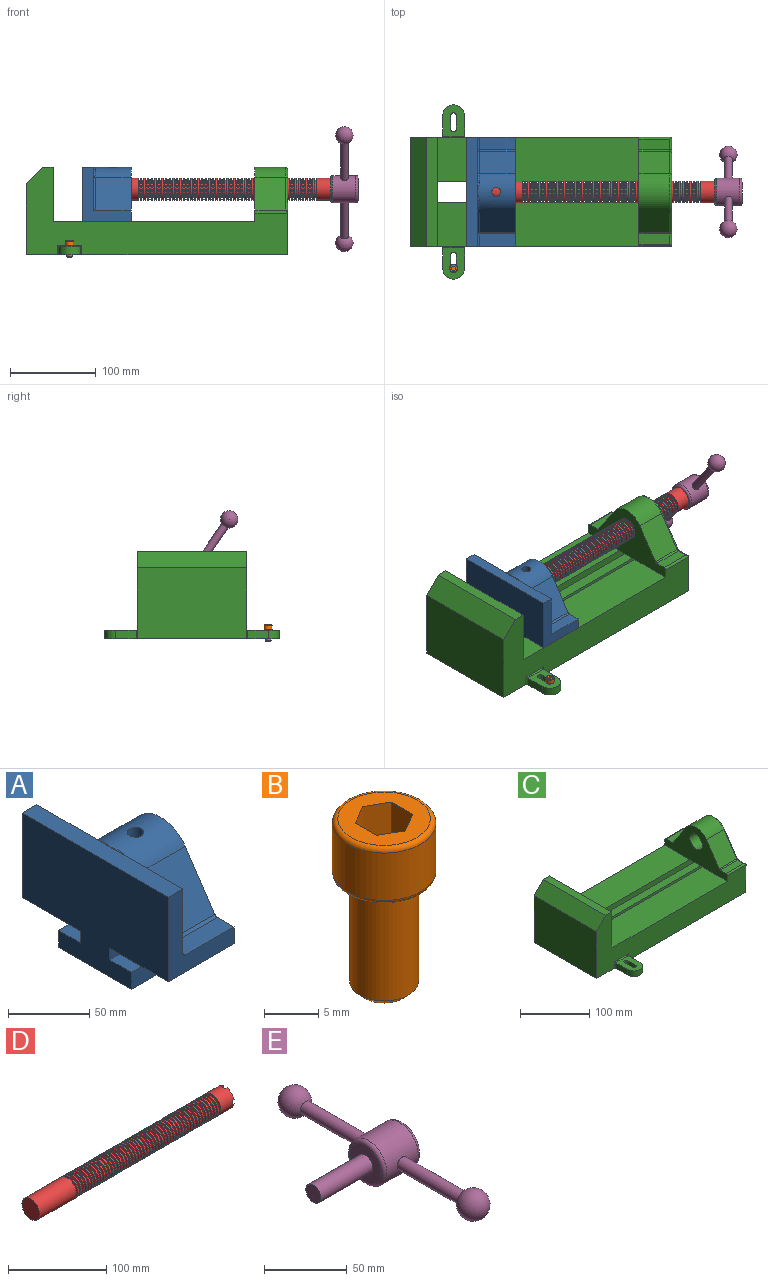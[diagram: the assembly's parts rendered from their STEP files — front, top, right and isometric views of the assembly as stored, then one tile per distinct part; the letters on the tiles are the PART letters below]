
ASSEMBLY  parts=5 mates=5
PART A: 36 faces, bbox 57.2x127x89 mm
  f0: plane 57.15x50.8mm, normal (0,0,-1), area 2903.2mm2, adj f6,f9,f10,f23
  f1: cylinder r=12.7mm len=44.45mm, axis (1,0,0), area 3464.3mm2, adj f6,f15,f16
  f2: plane 41.91x14.52mm, normal (0,0,1), area 608.5mm2, adj f6,f11,f24,f25
  f3: plane 51.86x48.26mm, normal (1,0,0), area 1495.7mm2, adj f8,f10,f31,f33,f35
  f4: plane 51.86x48.26mm, normal (1,0,0), area 1495.7mm2, adj f8,f11,f24,f28,f29
  f5: plane 57.15x50.8mm, normal (0,0,-1), area 2903.2mm2, adj f6,f9,f11,f22
  f6: plane 127x85.09mm, normal (1,0,0), area 5190.6mm2, adj f0,f1,f2,f5,f7,f10,f11,f12
  f7: plane 41.91x14.52mm, normal (0,0,1), area 608.5mm2, adj f6,f10,f30,f31
  f8: plane 127x12.7mm, normal (0,0,1), area 1612.9mm2, adj f3,f4,f9,f10,f11,f26,f34
  f9: plane 127x85.09mm, normal (-1,0,0), area 9096.8mm2, adj f0,f5,f8,f10,f11,f17,f18,f19
  f10: plane 63.5x57.15mm, normal (0,-1,0), area 1372.3mm2, adj f0,f3,f6,f7,f8,f9,f31
  f11: plane 63.5x57.15mm, normal (0,1,0), area 1372.3mm2, adj f2,f4,f5,f6,f8,f9,f24
  f12: plane 41.91x38.43mm, normal (0,-0.83,0.56), area 1939.2mm2, adj f6,f13,f30,f33
  f13: cylinder r=25.4mm len=44.45mm, axis (1,0,0), area 2026.5mm2, adj f6,f12,f14,f16,f26,f28,f34,f35
  f14: plane 41.91x38.43mm, normal (0,0.83,0.56), area 1939.2mm2, adj f6,f13,f25,f29
  f15: plane 25.4x25.4mm, normal (1,0,0), area 506.7mm2, adj f1
  f16: cylinder r=5.08mm len=13.76mm, axis (0,0,1), area 414mm2, adj f1,f13
  f17: plane 57.15x19.05mm, normal (0,0,1), area 1088.7mm2, adj f6,f9,f18,f23
  f18: plane 57.15x12.7mm, normal (0,-1,0), area 725.8mm2, adj f6,f9,f17,f19
  f19: plane 63.5x57.15mm, normal (0,0,-1), area 3629mm2, adj f6,f9,f18,f20
  f20: plane 57.15x12.7mm, normal (0,1,0), area 725.8mm2, adj f6,f9,f19,f21
  f21: plane 57.15x19.05mm, normal (0,0,1), area 1088.7mm2, adj f6,f9,f20,f22
  f22: plane 57.15x8.89mm, normal (0,1,0), area 508.1mm2, adj f5,f6,f9,f21
  f23: plane 57.15x8.89mm, normal (0,-1,0), area 508.1mm2, adj f0,f6,f9,f17
  f24: cylinder r=2.54mm len=14.52mm, axis (0,-1,0), area 57.9mm2, adj f2,f4,f11,f27
  f25: cylinder r=2.54mm len=41.91mm, axis (1,0,0), area 104.3mm2, adj f2,f6,f14,f27
  f26: bspline ~12.24x2.8mm, area 20.9mm2, adj f8,f13,f28
  f27: sphere r=2.54mm, area 6.3mm2, adj f24,f25,f29
  f28: torus R=27.94mm, axis (1,0,0), area 57.8mm2, adj f4,f13,f26,f29
  f29: cylinder r=2.54mm len=39.84mm, axis (0,-0.56,0.83), area 184.6mm2, adj f4,f14,f27,f28
  f30: cylinder r=2.54mm len=41.91mm, axis (1,0,0), area 104.3mm2, adj f6,f7,f12,f32
  f31: cylinder r=2.54mm len=14.52mm, axis (0,-1,0), area 57.9mm2, adj f3,f7,f10,f32
  f32: sphere r=2.54mm, area 6.3mm2, adj f30,f31,f33
  f33: cylinder r=2.54mm len=39.84mm, axis (0,-0.56,-0.83), area 184.6mm2, adj f3,f12,f32,f35
  f34: bspline ~12.24x2.8mm, area 20.9mm2, adj f8,f13,f35
  f35: torus R=27.94mm, axis (1,0,0), area 57.8mm2, adj f3,f13,f33,f34
PART B: 15 faces, bbox 10.3x10.3x19.1 mm
  f0: plane 8.51x8.51mm, normal (0,0,1), area 37.2mm2, adj f5,f6,f7,f8,f9,f10,f14
  f1: cylinder r=3.17mm len=11.94mm, axis (0,0,1), area 238.2mm2, adj f4,f12
  f2: plane 4.83x4.83mm, normal (0,0,-1), area 18.3mm2, adj f12
  f3: cylinder r=4.76mm len=9.53mm, axis (0,0,-1), area 159.6mm2, adj f13,f14
  f4: plane 8.51x8.51mm, normal (0,0,-1), area 25.2mm2, adj f1,f13
  f5: plane 4.83x2.38mm, normal (-0.5,-0.87,0), area 13.3mm2, adj f0,f6,f10,f11
  f6: plane 4.83x2.38mm, normal (0.5,-0.87,0), area 13.3mm2, adj f0,f5,f7,f11
  f7: plane 4.83x2.75mm, normal (1,0,0), area 13.3mm2, adj f0,f6,f8,f11
  f8: plane 4.83x2.38mm, normal (0.5,0.87,0), area 13.3mm2, adj f0,f7,f9,f11
  f9: plane 4.83x2.38mm, normal (-0.5,0.87,0), area 13.3mm2, adj f0,f8,f10,f11
  f10: plane 4.83x2.75mm, normal (-1,0,0), area 13.3mm2, adj f0,f5,f9,f11
  f11: plane 5.5x4.76mm, normal (0,0,1), area 19.6mm2, adj f5,f6,f7,f8,f9,f10
  f12: cone r=3.17mm half-angle=45deg, axis (0,0,1), area 18.9mm2, adj f1,f2
  f13: torus R=4.25mm, axis (0,0,1), area 23mm2, adj f3,f4
  f14: torus R=4.25mm, axis (0,0,1), area 23mm2, adj f0,f3
PART C: 61 faces, bbox 304.8x203.2x103.7 mm
  f0: plane 304.8x101.6mm, normal (0,1,0), area 13520.3mm2, adj f3,f4,f5,f6,f7,f8,f9,f16
  f1: plane 304.8x101.6mm, normal (0,-1,0), area 13520.3mm2, adj f2,f3,f5,f6,f7,f8,f9,f16
  f2: plane 234.95x50.8mm, normal (0,0,1), area 11935.5mm2, adj f1,f5,f16,f26
  f3: plane 127x99.06mm, normal (1,0,0), area 7097.5mm2, adj f0,f1,f9,f14,f17,f18,f19,f20
  f4: plane 234.95x50.8mm, normal (0,0,1), area 11935.5mm2, adj f0,f5,f16,f27
  f5: plane 127x101.6mm, normal (1,0,0), area 9516.1mm2, adj f0,f1,f2,f4,f6,f9,f18,f19
  f6: plane 127x12.7mm, normal (0,0,1), area 1612.9mm2, adj f0,f1,f5,f7
  f7: plane 127x19.05mm, normal (-0.71,0,0.71), area 3421.5mm2, adj f0,f1,f6,f8
  f8: plane 127x82.55mm, normal (-1,0,0), area 10483.8mm2, adj f0,f1,f7,f9
  f9: plane 304.8x203.2mm, normal (0,0,-1), area 33298.3mm2, adj f0,f1,f3,f5,f8,f21,f22,f39
  f10: plane 35.56x11.98mm, normal (0,0,1), area 426mm2, adj f16,f28,f29,f30
  f11: plane 38.43x35.56mm, normal (0,0.83,0.56), area 1645.4mm2, adj f12,f16,f29,f32
  f12: cylinder r=25.4mm len=42.19mm, axis (1,0,0), area 1770.2mm2, adj f11,f13,f16,f33
  f13: plane 38.43x35.56mm, normal (0,-0.83,0.56), area 1645.4mm2, adj f12,f16,f34,f35
  f14: cylinder r=12.7mm len=38.1mm, axis (1,0,0), area 3040.2mm2, adj f3,f16
  f15: plane 35.56x11.98mm, normal (0,0,1), area 426mm2, adj f16,f34,f36,f38
  f16: plane 127x63.5mm, normal (-1,0,0), area 4155.5mm2, adj f0,f1,f2,f4,f10,f11,f12,f13
  f17: plane 38.1x25.4mm, normal (0,0,-1), area 967.7mm2, adj f3,f16,f26,f27
  f18: plane 273.05x19.05mm, normal (0,0,-1), area 5201.6mm2, adj f3,f5,f19,f26
  f19: plane 273.05x12.7mm, normal (0,1,0), area 3467.7mm2, adj f3,f5,f18,f20
  f20: plane 273.05x19.05mm, normal (0,0,1), area 5201.6mm2, adj f3,f5,f19,f21
  f21: plane 273.05x16.51mm, normal (0,1,0), area 4508.1mm2, adj f3,f5,f9,f20
  f22: plane 273.05x16.51mm, normal (0,-1,0), area 4508.1mm2, adj f3,f5,f9,f23
  f23: plane 273.05x19.05mm, normal (0,0,1), area 5201.6mm2, adj f3,f5,f22,f24
  f24: plane 273.05x12.7mm, normal (0,-1,0), area 3467.7mm2, adj f3,f5,f23,f25
  f25: plane 273.05x19.05mm, normal (0,0,-1), area 5201.6mm2, adj f3,f5,f24,f27
  f26: plane 273.05x8.89mm, normal (0,1,0), area 2427.4mm2, adj f2,f3,f5,f17,f18
  f27: plane 273.05x8.89mm, normal (0,-1,0), area 2427.4mm2, adj f3,f4,f5,f17,f25
  f28: cylinder r=2.54mm len=38.1mm, axis (1,0,0), area 148.3mm2, adj f0,f10,f16,f30
  f29: cylinder r=2.54mm len=35.56mm, axis (-1,0,0), area 88.5mm2, adj f10,f11,f16,f31
  f30: cylinder r=2.54mm len=14.52mm, axis (0,1,0), area 54.3mm2, adj f3,f10,f28,f31
  f31: torus R=5.08mm, axis (-1,0,0), area 13.5mm2, adj f3,f29,f30,f32
  f32: cylinder r=2.54mm len=39.84mm, axis (0,0.56,-0.83), area 184.6mm2, adj f3,f11,f31,f33
  f33: torus R=22.86mm, axis (-1,0,0), area 191.4mm2, adj f3,f12,f32,f35
  f34: cylinder r=2.54mm len=35.56mm, axis (-1,0,0), area 88.5mm2, adj f13,f15,f16,f37
  f35: cylinder r=2.54mm len=39.84mm, axis (0,0.56,0.83), area 184.6mm2, adj f3,f13,f33,f37
  f36: cylinder r=2.54mm len=38.1mm, axis (-1,0,0), area 148.3mm2, adj f1,f15,f16,f38
  f37: torus R=5.08mm, axis (-1,0,0), area 13.5mm2, adj f3,f34,f35,f38
  f38: cylinder r=2.54mm len=14.52mm, axis (0,1,0), area 54.3mm2, adj f3,f15,f36,f37
  f39: plane 23.88x9.53mm, normal (-1,0,0), area 227.4mm2, adj f9,f45,f46,f60
  f40: plane 23.88x9.53mm, normal (1,0,0), area 227.4mm2, adj f9,f45,f46,f58
  f41: cylinder r=3.3mm len=9.53mm, axis (0,0,-1), area 98.8mm2, adj f9,f42,f44,f46
  f42: plane 15.62x9.53mm, normal (-1,0,0), area 148.8mm2, adj f9,f41,f43,f46
  f43: cylinder r=3.3mm len=9.53mm, axis (0,0,-1), area 98.8mm2, adj f9,f42,f44,f46
  f44: plane 15.62x9.53mm, normal (1,0,0), area 148.8mm2, adj f9,f41,f43,f46
  f45: cylinder r=12.7mm len=25.4mm, axis (0,0,-1), area 380mm2, adj f9,f39,f40,f46
  f46: plane 36.58x25.4mm, normal (0,0,1), area 722.4mm2, adj f39,f40,f41,f42,f43,f44,f45,f59
  f47: plane 23.88x9.53mm, normal (-1,0,0), area 227.4mm2, adj f9,f53,f54,f56
  f48: plane 23.88x9.53mm, normal (1,0,0), area 227.4mm2, adj f9,f53,f54,f55
  f49: cylinder r=3.3mm len=9.53mm, axis (0,0,-1), area 98.8mm2, adj f9,f50,f52,f54
  f50: plane 15.62x9.53mm, normal (-1,0,0), area 148.8mm2, adj f9,f49,f51,f54
  f51: cylinder r=3.3mm len=9.53mm, axis (0,0,-1), area 98.8mm2, adj f9,f50,f52,f54
  f52: plane 15.62x9.53mm, normal (1,0,0), area 148.8mm2, adj f9,f49,f51,f54
  f53: cylinder r=12.7mm len=25.4mm, axis (0,0,-1), area 380mm2, adj f9,f47,f48,f54
  f54: plane 36.58x25.4mm, normal (0,0,1), area 722.4mm2, adj f47,f48,f49,f50,f51,f52,f53,f57
  f55: cylinder r=1.52mm len=11.05mm, axis (0,0,-1), area 24.1mm2, adj f0,f9,f48,f57
  f56: cylinder r=1.52mm len=11.05mm, axis (0,0,1), area 24.1mm2, adj f0,f9,f47,f57
  f57: cylinder r=1.52mm len=28.45mm, axis (1,0,0), area 63.5mm2, adj f0,f54,f55,f56
  f58: cylinder r=1.52mm len=11.05mm, axis (0,0,1), area 24.1mm2, adj f1,f9,f40,f59
  f59: cylinder r=1.52mm len=28.45mm, axis (-1,0,0), area 63.5mm2, adj f1,f46,f58,f60
  f60: cylinder r=1.52mm len=11.05mm, axis (0,0,-1), area 24.1mm2, adj f1,f9,f39,f59
PART D: 220 faces, bbox 279.4x25.4x25.4 mm
  f0: cylinder r=12.7mm len=25.4mm, axis (-1,0,0), area 1468.2mm2, adj f1,f2,f3,f5,f7,f208,f209,f210
  f1: plane 9.9x9.9mm, normal (1,0,0), area 62.3mm2, adj f0,f4,f213,f216
  f2: plane 9.9x9.9mm, normal (1,0,0), area 62.3mm2, adj f0,f4,f210,f218
  f3: plane 9.9x9.9mm, normal (1,0,0), area 62.3mm2, adj f0,f4,f209,f212
  f4: cylinder r=6.35mm len=25.4mm, axis (1,0,0), area 960.3mm2, adj f1,f2,f3,f5,f6,f208,f209,f210
  f5: plane 9.9x9.9mm, normal (1,0,0), area 62.3mm2, adj f0,f4,f215,f217
  f6: plane 12.7x12.7mm, normal (1,0,0), area 126.7mm2, adj f4
  f7: cone r=12.7mm half-angle=76deg, axis (1,0,0), area 188mm2, adj f0,f9
  f8: cone r=10.16mm half-angle=76deg, axis (-1,0,0), area 188mm2, adj f9,f10
  f9: cylinder r=10.16mm len=20.32mm, axis (1,0,0), area 81.1mm2, adj f7,f8
  f10: cylinder r=12.7mm len=25.4mm, axis (-1,0,0), area 131.7mm2, adj f8,f11
  f11: cone r=12.7mm half-angle=76deg, axis (1,0,0), area 188mm2, adj f10,f13
  f12: cone r=10.16mm half-angle=76deg, axis (-1,0,0), area 188mm2, adj f13,f14
  f13: cylinder r=10.16mm len=20.32mm, axis (1,0,0), area 81.1mm2, adj f11,f12
  f14: cylinder r=12.7mm len=25.4mm, axis (-1,0,0), area 131.7mm2, adj f12,f15
  f15: cone r=12.7mm half-angle=76deg, axis (1,0,0), area 188mm2, adj f14,f17
  f16: cone r=10.16mm half-angle=76deg, axis (-1,0,0), area 188mm2, adj f17,f18
  f17: cylinder r=10.16mm len=20.32mm, axis (1,0,0), area 81.1mm2, adj f15,f16
  f18: cylinder r=12.7mm len=25.4mm, axis (-1,0,0), area 131.7mm2, adj f16,f19
  f19: cone r=12.7mm half-angle=76deg, axis (1,0,0), area 188mm2, adj f18,f21
  f20: cone r=10.16mm half-angle=76deg, axis (-1,0,0), area 188mm2, adj f21,f22
  f21: cylinder r=10.16mm len=20.32mm, axis (1,0,0), area 81.1mm2, adj f19,f20
  f22: cylinder r=12.7mm len=25.4mm, axis (-1,0,0), area 131.7mm2, adj f20,f23
  f23: cone r=12.7mm half-angle=76deg, axis (1,0,0), area 188mm2, adj f22,f25
  f24: cone r=10.16mm half-angle=76deg, axis (-1,0,0), area 188mm2, adj f25,f26
  f25: cylinder r=10.16mm len=20.32mm, axis (1,0,0), area 81.1mm2, adj f23,f24
  f26: cylinder r=12.7mm len=25.4mm, axis (-1,0,0), area 131.7mm2, adj f24,f27
  f27: cone r=12.7mm half-angle=76deg, axis (1,0,0), area 188mm2, adj f26,f29
  f28: cone r=10.16mm half-angle=76deg, axis (-1,0,0), area 188mm2, adj f29,f30
  f29: cylinder r=10.16mm len=20.32mm, axis (1,0,0), area 81.1mm2, adj f27,f28
  f30: cylinder r=12.7mm len=25.4mm, axis (-1,0,0), area 131.7mm2, adj f28,f31
  f31: cone r=12.7mm half-angle=76deg, axis (1,0,0), area 188mm2, adj f30,f33
  f32: cone r=10.16mm half-angle=76deg, axis (-1,0,0), area 188mm2, adj f33,f34
  f33: cylinder r=10.16mm len=20.32mm, axis (1,0,0), area 81.1mm2, adj f31,f32
  f34: cylinder r=12.7mm len=25.4mm, axis (-1,0,0), area 131.7mm2, adj f32,f35
  f35: cone r=12.7mm half-angle=76deg, axis (1,0,0), area 188mm2, adj f34,f37
  f36: cone r=10.16mm half-angle=76deg, axis (-1,0,0), area 188mm2, adj f37,f38
  f37: cylinder r=10.16mm len=20.32mm, axis (1,0,0), area 81.1mm2, adj f35,f36
  f38: cylinder r=12.7mm len=25.4mm, axis (-1,0,0), area 131.7mm2, adj f36,f39
  f39: cone r=12.7mm half-angle=76deg, axis (1,0,0), area 188mm2, adj f38,f41
  f40: cone r=10.16mm half-angle=76deg, axis (-1,0,0), area 188mm2, adj f41,f42
  f41: cylinder r=10.16mm len=20.32mm, axis (1,0,0), area 81.1mm2, adj f39,f40
  f42: cylinder r=12.7mm len=25.4mm, axis (-1,0,0), area 131.7mm2, adj f40,f43
  f43: cone r=12.7mm half-angle=76deg, axis (1,0,0), area 188mm2, adj f42,f45
  f44: cone r=10.16mm half-angle=76deg, axis (-1,0,0), area 188mm2, adj f45,f46
  f45: cylinder r=10.16mm len=20.32mm, axis (1,0,0), area 81.1mm2, adj f43,f44
  f46: cylinder r=12.7mm len=25.4mm, axis (-1,0,0), area 131.7mm2, adj f44,f47
  f47: cone r=12.7mm half-angle=76deg, axis (1,0,0), area 188mm2, adj f46,f49
  f48: cone r=10.16mm half-angle=76deg, axis (-1,0,0), area 188mm2, adj f49,f50
  f49: cylinder r=10.16mm len=20.32mm, axis (1,0,0), area 81.1mm2, adj f47,f48
  f50: cylinder r=12.7mm len=25.4mm, axis (-1,0,0), area 131.7mm2, adj f48,f51
  f51: cone r=12.7mm half-angle=76deg, axis (1,0,0), area 188mm2, adj f50,f53
  f52: cone r=10.16mm half-angle=76deg, axis (-1,0,0), area 188mm2, adj f53,f54
  f53: cylinder r=10.16mm len=20.32mm, axis (1,0,0), area 81.1mm2, adj f51,f52
  f54: cylinder r=12.7mm len=25.4mm, axis (-1,0,0), area 131.7mm2, adj f52,f55
  f55: cone r=12.7mm half-angle=76deg, axis (1,0,0), area 188mm2, adj f54,f57
  f56: cone r=10.16mm half-angle=76deg, axis (-1,0,0), area 188mm2, adj f57,f58
  f57: cylinder r=10.16mm len=20.32mm, axis (1,0,0), area 81.1mm2, adj f55,f56
  f58: cylinder r=12.7mm len=25.4mm, axis (-1,0,0), area 131.7mm2, adj f56,f59
  f59: cone r=12.7mm half-angle=76deg, axis (1,0,0), area 188mm2, adj f58,f61
  f60: cone r=10.16mm half-angle=76deg, axis (-1,0,0), area 188mm2, adj f61,f62
  f61: cylinder r=10.16mm len=20.32mm, axis (1,0,0), area 81.1mm2, adj f59,f60
  f62: cylinder r=12.7mm len=25.4mm, axis (-1,0,0), area 131.7mm2, adj f60,f63
  f63: cone r=12.7mm half-angle=76deg, axis (1,0,0), area 188mm2, adj f62,f65
  f64: cone r=10.16mm half-angle=76deg, axis (-1,0,0), area 188mm2, adj f65,f66
  f65: cylinder r=10.16mm len=20.32mm, axis (1,0,0), area 81.1mm2, adj f63,f64
  f66: cylinder r=12.7mm len=25.4mm, axis (-1,0,0), area 131.7mm2, adj f64,f67
  f67: cone r=12.7mm half-angle=76deg, axis (1,0,0), area 188mm2, adj f66,f69
  f68: cone r=10.16mm half-angle=76deg, axis (-1,0,0), area 188mm2, adj f69,f70
  f69: cylinder r=10.16mm len=20.32mm, axis (1,0,0), area 81.1mm2, adj f67,f68
  f70: cylinder r=12.7mm len=25.4mm, axis (-1,0,0), area 131.7mm2, adj f68,f71
  f71: cone r=12.7mm half-angle=76deg, axis (1,0,0), area 188mm2, adj f70,f73
  f72: cone r=10.16mm half-angle=76deg, axis (-1,0,0), area 188mm2, adj f73,f74
  f73: cylinder r=10.16mm len=20.32mm, axis (1,0,0), area 81.1mm2, adj f71,f72
  f74: cylinder r=12.7mm len=25.4mm, axis (-1,0,0), area 131.7mm2, adj f72,f75
  f75: cone r=12.7mm half-angle=76deg, axis (1,0,0), area 188mm2, adj f74,f77
  f76: cone r=10.16mm half-angle=76deg, axis (-1,0,0), area 188mm2, adj f77,f78
  f77: cylinder r=10.16mm len=20.32mm, axis (1,0,0), area 81.1mm2, adj f75,f76
  f78: cylinder r=12.7mm len=25.4mm, axis (-1,0,0), area 131.7mm2, adj f76,f79
  f79: cone r=12.7mm half-angle=76deg, axis (1,0,0), area 188mm2, adj f78,f81
  f80: cone r=10.16mm half-angle=76deg, axis (-1,0,0), area 188mm2, adj f81,f82
  f81: cylinder r=10.16mm len=20.32mm, axis (1,0,0), area 81.1mm2, adj f79,f80
  f82: cylinder r=12.7mm len=25.4mm, axis (-1,0,0), area 131.7mm2, adj f80,f83
  f83: cone r=12.7mm half-angle=76deg, axis (1,0,0), area 188mm2, adj f82,f85
  f84: cone r=10.16mm half-angle=76deg, axis (-1,0,0), area 188mm2, adj f85,f86
  f85: cylinder r=10.16mm len=20.32mm, axis (1,0,0), area 81.1mm2, adj f83,f84
  f86: cylinder r=12.7mm len=25.4mm, axis (-1,0,0), area 131.7mm2, adj f84,f87
  f87: cone r=12.7mm half-angle=76deg, axis (1,0,0), area 188mm2, adj f86,f89
  f88: cone r=10.16mm half-angle=76deg, axis (-1,0,0), area 188mm2, adj f89,f90
  f89: cylinder r=10.16mm len=20.32mm, axis (1,0,0), area 81.1mm2, adj f87,f88
  f90: cylinder r=12.7mm len=25.4mm, axis (-1,0,0), area 131.7mm2, adj f88,f91
  f91: cone r=12.7mm half-angle=76deg, axis (1,0,0), area 188mm2, adj f90,f93
  f92: cone r=10.16mm half-angle=76deg, axis (-1,0,0), area 188mm2, adj f93,f94
  f93: cylinder r=10.16mm len=20.32mm, axis (1,0,0), area 81.1mm2, adj f91,f92
  f94: cylinder r=12.7mm len=25.4mm, axis (-1,0,0), area 131.7mm2, adj f92,f95
  f95: cone r=12.7mm half-angle=76deg, axis (1,0,0), area 188mm2, adj f94,f97
  f96: cone r=10.16mm half-angle=76deg, axis (-1,0,0), area 188mm2, adj f97,f98
  f97: cylinder r=10.16mm len=20.32mm, axis (1,0,0), area 81.1mm2, adj f95,f96
  f98: cylinder r=12.7mm len=25.4mm, axis (-1,0,0), area 131.7mm2, adj f96,f99
  f99: cone r=12.7mm half-angle=76deg, axis (1,0,0), area 188mm2, adj f98,f101
  f100: cone r=10.16mm half-angle=76deg, axis (-1,0,0), area 188mm2, adj f101,f102
  f101: cylinder r=10.16mm len=20.32mm, axis (1,0,0), area 81.1mm2, adj f99,f100
  f102: cylinder r=12.7mm len=25.4mm, axis (-1,0,0), area 131.7mm2, adj f100,f103
  f103: cone r=12.7mm half-angle=76deg, axis (1,0,0), area 188mm2, adj f102,f105
  f104: cone r=10.16mm half-angle=76deg, axis (-1,0,0), area 188mm2, adj f105,f106
  f105: cylinder r=10.16mm len=20.32mm, axis (1,0,0), area 81.1mm2, adj f103,f104
  f106: cylinder r=12.7mm len=25.4mm, axis (-1,0,0), area 131.7mm2, adj f104,f107
  f107: cone r=12.7mm half-angle=76deg, axis (1,0,0), area 188mm2, adj f106,f109
  f108: cone r=10.16mm half-angle=76deg, axis (-1,0,0), area 188mm2, adj f109,f110
  f109: cylinder r=10.16mm len=20.32mm, axis (1,0,0), area 81.1mm2, adj f107,f108
  f110: cylinder r=12.7mm len=25.4mm, axis (-1,0,0), area 131.7mm2, adj f108,f111
  f111: cone r=12.7mm half-angle=76deg, axis (1,0,0), area 188mm2, adj f110,f113
  f112: cone r=10.16mm half-angle=76deg, axis (-1,0,0), area 188mm2, adj f113,f114
  f113: cylinder r=10.16mm len=20.32mm, axis (1,0,0), area 81.1mm2, adj f111,f112
  f114: cylinder r=12.7mm len=25.4mm, axis (-1,0,0), area 131.7mm2, adj f112,f115
  f115: cone r=12.7mm half-angle=76deg, axis (1,0,0), area 188mm2, adj f114,f117
  f116: cone r=10.16mm half-angle=76deg, axis (-1,0,0), area 188mm2, adj f117,f118
  f117: cylinder r=10.16mm len=20.32mm, axis (1,0,0), area 81.1mm2, adj f115,f116
  f118: cylinder r=12.7mm len=25.4mm, axis (-1,0,0), area 131.7mm2, adj f116,f119
  f119: cone r=12.7mm half-angle=76deg, axis (1,0,0), area 188mm2, adj f118,f121
  f120: cone r=10.16mm half-angle=76deg, axis (-1,0,0), area 188mm2, adj f121,f122
  f121: cylinder r=10.16mm len=20.32mm, axis (1,0,0), area 81.1mm2, adj f119,f120
  f122: cylinder r=12.7mm len=25.4mm, axis (-1,0,0), area 131.7mm2, adj f120,f123
  f123: cone r=12.7mm half-angle=76deg, axis (1,0,0), area 188mm2, adj f122,f125
  f124: cone r=10.16mm half-angle=76deg, axis (-1,0,0), area 188mm2, adj f125,f126
  f125: cylinder r=10.16mm len=20.32mm, axis (1,0,0), area 81.1mm2, adj f123,f124
  f126: cylinder r=12.7mm len=25.4mm, axis (-1,0,0), area 131.7mm2, adj f124,f127
  f127: cone r=12.7mm half-angle=76deg, axis (1,0,0), area 188mm2, adj f126,f129
  f128: cone r=10.16mm half-angle=76deg, axis (-1,0,0), area 188mm2, adj f129,f130
  f129: cylinder r=10.16mm len=20.32mm, axis (1,0,0), area 81.1mm2, adj f127,f128
  f130: cylinder r=12.7mm len=25.4mm, axis (-1,0,0), area 131.7mm2, adj f128,f131
  f131: cone r=12.7mm half-angle=76deg, axis (1,0,0), area 188mm2, adj f130,f133
  f132: cone r=10.16mm half-angle=76deg, axis (-1,0,0), area 188mm2, adj f133,f134
  f133: cylinder r=10.16mm len=20.32mm, axis (1,0,0), area 81.1mm2, adj f131,f132
  f134: cylinder r=12.7mm len=25.4mm, axis (-1,0,0), area 131.7mm2, adj f132,f135
  f135: cone r=12.7mm half-angle=76deg, axis (1,0,0), area 188mm2, adj f134,f137
  f136: cone r=10.16mm half-angle=76deg, axis (-1,0,0), area 188mm2, adj f137,f138
  f137: cylinder r=10.16mm len=20.32mm, axis (1,0,0), area 81.1mm2, adj f135,f136
  f138: cylinder r=12.7mm len=25.4mm, axis (-1,0,0), area 131.7mm2, adj f136,f139
  f139: cone r=12.7mm half-angle=76deg, axis (1,0,0), area 188mm2, adj f138,f141
  f140: cone r=10.16mm half-angle=76deg, axis (-1,0,0), area 188mm2, adj f141,f142
  f141: cylinder r=10.16mm len=20.32mm, axis (1,0,0), area 81.1mm2, adj f139,f140
  f142: cylinder r=12.7mm len=25.4mm, axis (-1,0,0), area 131.7mm2, adj f140,f143
  f143: cone r=12.7mm half-angle=76deg, axis (1,0,0), area 188mm2, adj f142,f145
  f144: cone r=10.16mm half-angle=76deg, axis (-1,0,0), area 188mm2, adj f145,f146
  f145: cylinder r=10.16mm len=20.32mm, axis (1,0,0), area 81.1mm2, adj f143,f144
  f146: cylinder r=12.7mm len=25.4mm, axis (-1,0,0), area 131.7mm2, adj f144,f147
  f147: cone r=12.7mm half-angle=76deg, axis (1,0,0), area 188mm2, adj f146,f149
  f148: cone r=10.16mm half-angle=76deg, axis (-1,0,0), area 188mm2, adj f149,f150
  f149: cylinder r=10.16mm len=20.32mm, axis (1,0,0), area 81.1mm2, adj f147,f148
  f150: cylinder r=12.7mm len=25.4mm, axis (-1,0,0), area 131.7mm2, adj f148,f151
  f151: cone r=12.7mm half-angle=76deg, axis (1,0,0), area 188mm2, adj f150,f153
  f152: cone r=10.16mm half-angle=76deg, axis (-1,0,0), area 188mm2, adj f153,f154
  f153: cylinder r=10.16mm len=20.32mm, axis (1,0,0), area 81.1mm2, adj f151,f152
  f154: cylinder r=12.7mm len=25.4mm, axis (-1,0,0), area 131.7mm2, adj f152,f155
  f155: cone r=12.7mm half-angle=76deg, axis (1,0,0), area 188mm2, adj f154,f157
  f156: cone r=10.16mm half-angle=76deg, axis (-1,0,0), area 188mm2, adj f157,f158
  f157: cylinder r=10.16mm len=20.32mm, axis (1,0,0), area 81.1mm2, adj f155,f156
  f158: cylinder r=12.7mm len=25.4mm, axis (-1,0,0), area 131.7mm2, adj f156,f159
  f159: cone r=12.7mm half-angle=76deg, axis (1,0,0), area 188mm2, adj f158,f161
  f160: cone r=10.16mm half-angle=76deg, axis (-1,0,0), area 188mm2, adj f161,f162
  f161: cylinder r=10.16mm len=20.32mm, axis (1,0,0), area 81.1mm2, adj f159,f160
  f162: cylinder r=12.7mm len=25.4mm, axis (-1,0,0), area 131.7mm2, adj f160,f163
  f163: cone r=12.7mm half-angle=76deg, axis (1,0,0), area 188mm2, adj f162,f165
  f164: cone r=10.16mm half-angle=76deg, axis (-1,0,0), area 188mm2, adj f165,f166
  f165: cylinder r=10.16mm len=20.32mm, axis (1,0,0), area 81.1mm2, adj f163,f164
  f166: cylinder r=12.7mm len=25.4mm, axis (-1,0,0), area 131.7mm2, adj f164,f167
  f167: cone r=12.7mm half-angle=76deg, axis (1,0,0), area 188mm2, adj f166,f169
  f168: cone r=10.16mm half-angle=76deg, axis (-1,0,0), area 188mm2, adj f169,f170
  f169: cylinder r=10.16mm len=20.32mm, axis (1,0,0), area 81.1mm2, adj f167,f168
  f170: cylinder r=12.7mm len=25.4mm, axis (-1,0,0), area 131.7mm2, adj f168,f171
  f171: cone r=12.7mm half-angle=76deg, axis (1,0,0), area 188mm2, adj f170,f173
  f172: cone r=10.16mm half-angle=76deg, axis (-1,0,0), area 188mm2, adj f173,f174
  f173: cylinder r=10.16mm len=20.32mm, axis (1,0,0), area 81.1mm2, adj f171,f172
  f174: cylinder r=12.7mm len=25.4mm, axis (-1,0,0), area 131.7mm2, adj f172,f175
  f175: cone r=12.7mm half-angle=76deg, axis (1,0,0), area 188mm2, adj f174,f177
  f176: cone r=10.16mm half-angle=76deg, axis (-1,0,0), area 188mm2, adj f177,f178
  f177: cylinder r=10.16mm len=20.32mm, axis (1,0,0), area 81.1mm2, adj f175,f176
  f178: cylinder r=12.7mm len=25.4mm, axis (-1,0,0), area 131.7mm2, adj f176,f179
  f179: cone r=12.7mm half-angle=76deg, axis (1,0,0), area 188mm2, adj f178,f181
  f180: cone r=10.16mm half-angle=76deg, axis (-1,0,0), area 188mm2, adj f181,f182
  f181: cylinder r=10.16mm len=20.32mm, axis (1,0,0), area 81.1mm2, adj f179,f180
  f182: cylinder r=12.7mm len=25.4mm, axis (-1,0,0), area 131.7mm2, adj f180,f183
  f183: cone r=12.7mm half-angle=76deg, axis (1,0,0), area 188mm2, adj f182,f185
  f184: cone r=10.16mm half-angle=76deg, axis (-1,0,0), area 188mm2, adj f185,f186
  f185: cylinder r=10.16mm len=20.32mm, axis (1,0,0), area 81.1mm2, adj f183,f184
  f186: cylinder r=12.7mm len=25.4mm, axis (-1,0,0), area 131.7mm2, adj f184,f187
  f187: cone r=12.7mm half-angle=76deg, axis (1,0,0), area 188mm2, adj f186,f189
  f188: cone r=10.16mm half-angle=76deg, axis (-1,0,0), area 188mm2, adj f189,f190
  f189: cylinder r=10.16mm len=20.32mm, axis (1,0,0), area 81.1mm2, adj f187,f188
  f190: cylinder r=12.7mm len=25.4mm, axis (-1,0,0), area 131.7mm2, adj f188,f191
  f191: cone r=12.7mm half-angle=76deg, axis (1,0,0), area 188mm2, adj f190,f193
  f192: cone r=10.16mm half-angle=76deg, axis (-1,0,0), area 188mm2, adj f193,f194
  f193: cylinder r=10.16mm len=20.32mm, axis (1,0,0), area 81.1mm2, adj f191,f192
  f194: cylinder r=12.7mm len=25.4mm, axis (-1,0,0), area 131.7mm2, adj f192,f195
  f195: cone r=12.7mm half-angle=76deg, axis (1,0,0), area 188mm2, adj f194,f197
  f196: cone r=10.16mm half-angle=76deg, axis (-1,0,0), area 188mm2, adj f197,f198
  f197: cylinder r=10.16mm len=20.32mm, axis (1,0,0), area 81.1mm2, adj f195,f196
  f198: cylinder r=12.7mm len=25.4mm, axis (-1,0,0), area 131.7mm2, adj f196,f199
  f199: cone r=12.7mm half-angle=76deg, axis (1,0,0), area 188mm2, adj f198,f201
  f200: cone r=10.16mm half-angle=76deg, axis (-1,0,0), area 188mm2, adj f201,f202
  f201: cylinder r=10.16mm len=20.32mm, axis (1,0,0), area 81.1mm2, adj f199,f200
  f202: cylinder r=12.7mm len=25.4mm, axis (-1,0,0), area 131.7mm2, adj f200,f203
  f203: cone r=12.7mm half-angle=76deg, axis (1,0,0), area 188mm2, adj f202,f205
  f204: cone r=10.16mm half-angle=76deg, axis (-1,0,0), area 188mm2, adj f205,f207
  f205: cylinder r=10.16mm len=20.32mm, axis (1,0,0), area 81.1mm2, adj f203,f204
  f206: plane 25.4x25.4mm, normal (-1,0,0), area 506.7mm2, adj f207
  f207: cylinder r=12.7mm len=52.45mm, axis (-1,0,0), area 4185.4mm2, adj f204,f206
  f208: plane 6.88x5.08mm, normal (1,0,0), area 32.7mm2, adj f0,f4,f209,f210
  f209: plane 6.62x2.54mm, normal (0,-1,0), area 16.8mm2, adj f0,f3,f4,f208
  f210: plane 6.62x2.54mm, normal (0,1,0), area 16.8mm2, adj f0,f2,f4,f208
  f211: plane 6.88x5.08mm, normal (1,0,0), area 32.7mm2, adj f0,f4,f212,f213
  f212: plane 6.62x2.54mm, normal (0,0,1), area 16.8mm2, adj f0,f3,f4,f211
  f213: plane 6.62x2.54mm, normal (0,0,-1), area 16.8mm2, adj f0,f1,f4,f211
  f214: plane 6.88x5.08mm, normal (1,0,0), area 32.7mm2, adj f0,f4,f215,f216
  f215: plane 6.62x2.54mm, normal (0,1,0), area 16.8mm2, adj f0,f4,f5,f214
  f216: plane 6.62x2.54mm, normal (0,-1,0), area 16.8mm2, adj f0,f1,f4,f214
  f217: plane 6.62x2.54mm, normal (0,0,-1), area 16.8mm2, adj f0,f4,f5,f219
  f218: plane 6.62x2.54mm, normal (0,0,1), area 16.8mm2, adj f0,f2,f4,f219
  f219: plane 6.88x5.08mm, normal (1,0,0), area 32.7mm2, adj f0,f4,f217,f218
PART E: 11 faces, bbox 76.2x172.7x34.4 mm
  f0: sphere r=10.16mm, area 1231.8mm2, adj f1
  f1: cylinder r=4.45mm len=51.82mm, axis (0,1,0), area 1438.5mm2, adj f0,f4
  f2: sphere r=10.16mm, area 1231.8mm2, adj f3
  f3: cylinder r=4.45mm len=51.82mm, axis (0,1,0), area 1438.5mm2, adj f2,f4
  f4: cylinder r=15.88mm len=31.75mm, axis (-1,0,0), area 2534.7mm2, adj f1,f3,f9,f10
  f5: cylinder r=6.35mm len=44.45mm, axis (-1,0,0), area 1773.5mm2, adj f6,f8
  f6: plane 12.7x12.7mm, normal (-1,0,0), area 126.7mm2, adj f5
  f7: plane 26.67x26.67mm, normal (1,0,0), area 558.6mm2, adj f10
  f8: plane 26.67x26.67mm, normal (-1,0,0), area 432mm2, adj f5,f9
  f9: torus R=13.33mm, axis (1,0,0), area 374.8mm2, adj f4,f8
  f10: torus R=13.33mm, axis (1,0,0), area 374.8mm2, adj f4,f7
PLACE A t=(33.7,0,0)mm
PLACE B rot(axis=(0,0,1),90deg) t=(-254,-88.9,9.52)mm
PLACE C at identity fixed
PLACE D rot(axis=(-1,0,0),55.3deg) t=(33.7,-62.67,32.86)mm
PLACE E rot(axis=(-1,0,0),55.3deg) t=(12.11,-62.67,32.86)mm
MATE fastened D.f4 <-> E.f5  axis (1,0,0) through (50.21,0,76.2)mm
MATE planar A.f0 <-> C.f2  axis (0,0,-1) through (-210.77,-38.1,38.1)mm
MATE pin_slot B.f1 <-> C.f41  axis (0,0,1) through (-254,-88.9,9.52)mm
MATE revolute D.f7 <-> A.f28  axis (-1,0,0) through (-226.65,0,76.2)mm
MATE cylindrical C.f12 <-> D.f7  axis (-1,0,0) through (-38.1,0,76.2)mm
